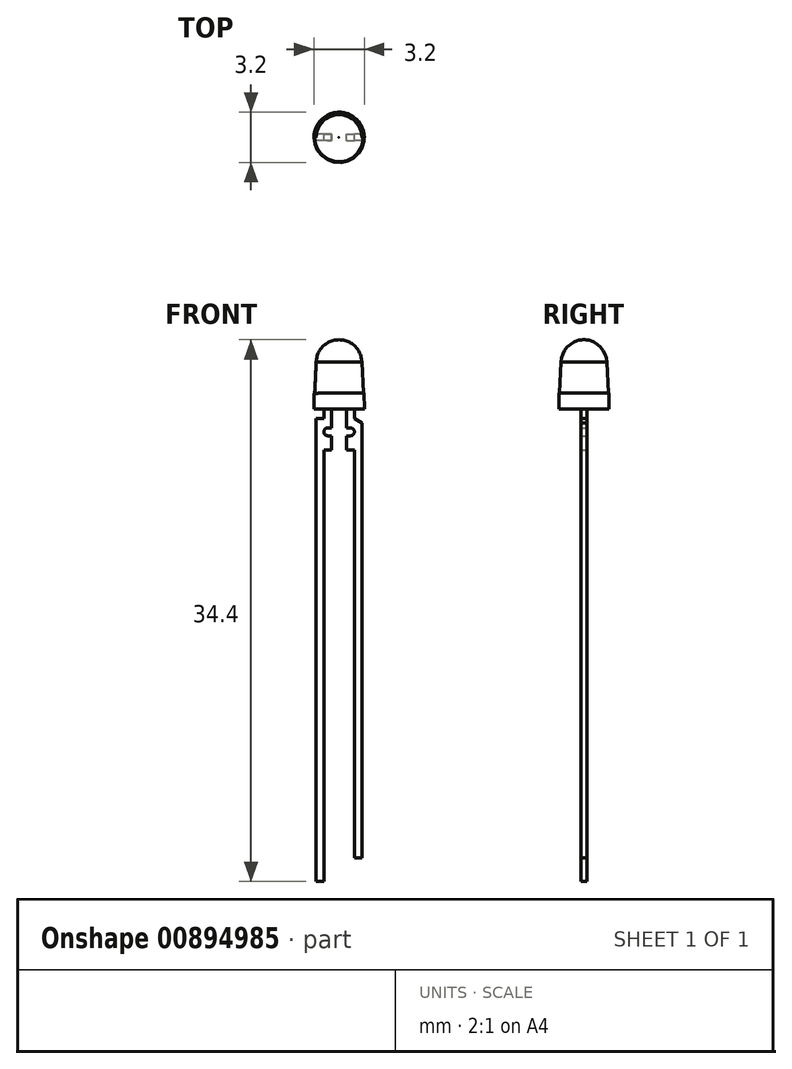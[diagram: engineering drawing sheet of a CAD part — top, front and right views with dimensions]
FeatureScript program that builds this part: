
annotation { "Feature Type Name" : "Feature", "Feature Type Description" : "" }
export const myFeature = defineFeature(function(context is Context, id is Id, definition is map)
    precondition{}
    {
        {
            var Q0;
            Q0=qCreatedBy(makeId("Front.planeOp"),FACE);
            var sketch = newSketch(context, id + "F0", { "sketchPlane" : qUnion([Q0])});
            skLineSegment(sketch, "E0", {"start": v(-1.6, -2.9) * mm, "end": v(0.47, -2.9) * mm});
            skLineSegment(sketch, "E1", {"start": v(1.6, -2.9) * mm, "end": v(1.6, -1.9) * mm});
            skLineSegment(sketch, "E2", {"start": v(1.6, -1.9) * mm, "end": v(1.55, -1.9) * mm});
            skLineSegment(sketch, "E3", {"start": v(-1.6, -2.9) * mm, "end": v(-1.6, -1.9) * mm});
            skLineSegment(sketch, "E4", {"start": v(-1.6, -1.9) * mm, "end": v(-1.55, -1.9) * mm});
            skLineSegment(sketch, "E5", {"start": v(0.47, -3.5) * mm, "end": v(0.47, -2.9) * mm});
            skLineSegment(sketch, "E6", {"start": v(-0.47, -3.5) * mm, "end": v(-0.47, -2.9) * mm});
            skLineSegment(sketch, "E7", {"start": v(-0.97, -3.5) * mm, "end": v(-0.97, -2.9) * mm});
            skLineSegment(sketch, "E8", {"start": v(0.97, -3.5) * mm, "end": v(0.97, -2.9) * mm});
            skLineSegment(sketch, "E9", {"start": v(0.47, -3.5) * mm, "end": v(0.47, -4.1) * mm});
            skLineSegment(sketch, "E10", {"start": v(-0.47, -3.5) * mm, "end": v(-0.47, -4.1) * mm});
            skLineSegment(sketch, "E11", {"start": v(-0.47, -5.5) * mm, "end": v(-0.97, -5.5) * mm});
            skLineSegment(sketch, "E12", {"start": v(0.47, -5.5) * mm, "end": v(0.97, -5.5) * mm});
            skLineSegment(sketch, "E13", {"start": v(-0.97, -3.5) * mm, "end": v(-1.47, -3.5) * mm});
            skLineSegment(sketch, "E14", {"start": v(-1.47, -3.5) * mm, "end": v(-1.47, -32.9) * mm});
            skLineSegment(sketch, "E15", {"start": v(-1.47, -32.9) * mm, "end": v(-0.97, -32.9) * mm});
            skLineSegment(sketch, "E16", {"start": v(-0.97, -32.9) * mm, "end": v(-0.97, -5.5) * mm});
            skLineSegment(sketch, "E17", {"start": v(1.47, -3.8) * mm, "end": v(1.47, -31.4) * mm});
            skLineSegment(sketch, "E18", {"start": v(1.47, -31.4) * mm, "end": v(0.97, -31.4) * mm});
            skLineSegment(sketch, "E19", {"start": v(0.97, -31.4) * mm, "end": v(0.97, -5.5) * mm});
            skLineSegment(sketch, "E20", {"start": v(1.47, -3.8) * mm, "end": v(0.97, -3.5) * mm});
            skLineSegment(sketch, "E21", {"start": v(0.47, -4.1) * mm, "end": v(0.72, -4.1) * mm});
            skLineSegment(sketch, "E22", {"start": v(0.72, -4.6) * mm, "end": v(0.47, -4.6) * mm});
            skLineSegment(sketch, "E23.trimOffspring", {"start": v(0.47, -4.6) * mm, "end": v(0.47, -5.5) * mm});
            skArc(sketch, "E24", {"start": v(0.72, -4.6) * mm, "mid": v(0.97, -4.35) * mm, "end": v(0.72, -4.1) * mm});
            skLineSegment(sketch, "E25", {"start": v(-0.47, -4.1) * mm, "end": v(-0.72, -4.1) * mm});
            skLineSegment(sketch, "E26", {"start": v(-0.72, -4.6) * mm, "end": v(-0.47, -4.6) * mm});
            skLineSegment(sketch, "E27.trimOffspring", {"start": v(-0.47, -4.6) * mm, "end": v(-0.47, -5.5) * mm});
            skArc(sketch, "E28", {"start": v(-0.72, -4.1) * mm, "mid": v(-0.97, -4.35) * mm, "end": v(-0.72, -4.6) * mm});
            skArc(sketch, "E29", {"start": v(1.45, 0.1) * mm, "mid": v(0, 1.5) * mm, "end": v(-1.45, 0.09) * mm});
            skLineSegment(sketch, "E30", {"start": v(0, -2.9) * mm, "end": v(0, 1.5) * mm});
            skLineSegment(sketch, "E31", {"start": v(1.55, -1.9) * mm, "end": v(1.45, 0.1) * mm});
            skLineSegment(sketch, "E32", {"start": v(-1.45, 0.09) * mm, "end": v(-1.55, -1.9) * mm});
            skLineSegment(sketch, "E33.trimOffspring", {"start": v(0.97, -2.9) * mm, "end": v(1.6, -2.9) * mm});
            skLineSegment(sketch, "E34", {"start": v(0.47, -2.9) * mm, "end": v(0.97, -2.9) * mm});
            skSolve(sketch);
        }
        {
            var Q0;
            {var subQ0=sQuery(id+"F0.wireOp",EDGE,"E3");Q0=makeQuery(id+"F0.imprint","IMPRINT",FACE,{"disambiguationData":[TD([[makeQuery(id+"F0.imprint","IMPRINT",EDGE,{"derivedFrom":subQ0}),-1.0]])]});}
            var Q1;
            Q1=sQuery(id+"F0.wireOp",EDGE,"E30");
            revolve(context, id + "F1", {"surfaceOperationType" : NewSurfaceOperationType.NEW, "entities" : qUnion([Q0]), "axis" : qUnion([Q1]), "revolveType" : RevolveType.FULL});
        }
        {
            var Q0;
            Q0=makeQuery(id+"F0.imprint","IMPRINT",FACE,{"disambiguationData":[TD([[makeQuery(id+"F0.imprint","IMPRINT",EDGE,{"derivedFrom":sQuery(id+"F0.wireOp",EDGE,"E5")}),-1.0]])]});
            var Q1;
            {var subQ0=sQuery(id+"F0.wireOp",EDGE,"E6");Q1=makeQuery(id+"F0.imprint","IMPRINT",FACE,{"disambiguationData":[TD([[makeQuery(id+"F0.imprint","IMPRINT",EDGE,{"derivedFrom":subQ0}),1.0]])]});}
            extrude(context, id + "F2", {"entities" : qUnion([Q0, Q1]), "operationType" : NewBodyOperationType.ADD, "endBound" : BoundingType.SYMMETRIC, "depth" : .4 * mm, "offsetDistance" : 25 * mm});
        }
    });
